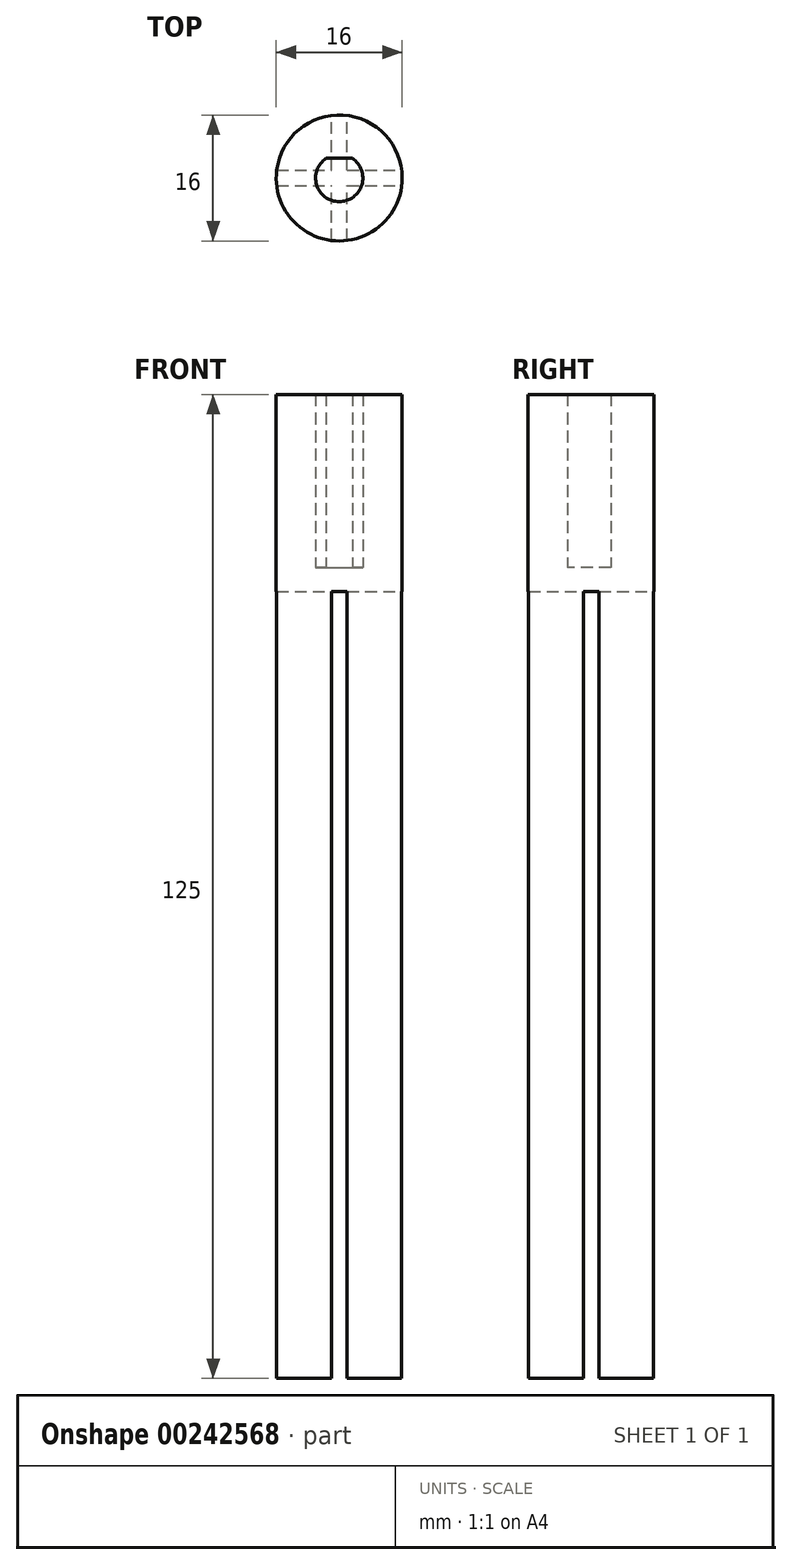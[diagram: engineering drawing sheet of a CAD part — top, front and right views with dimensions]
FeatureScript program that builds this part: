
annotation { "Feature Type Name" : "Feature", "Feature Type Description" : "" }
export const myFeature = defineFeature(function(context is Context, id is Id, definition is map)
    precondition{}
    {
        {
            var Q0;
            Q0=qCreatedBy(makeId("Top.planeOp"),FACE);
            var sketch = newSketch(context, id + "F0", { "sketchPlane" : qUnion([Q0])});
            skCircle(sketch, "E0", {"center": v(0, 0) * mm, "radius": 3 * mm});
            skLineSegment(sketch, "E1", {"start": v(-1.66, 2.5) * mm, "end": v(1.66, 2.5) * mm});
            skCircle(sketch, "E2", {"center": v(0, 0) * mm, "radius": 8 * mm});
            skSolve(sketch);
        }
        {
            var Q0;
            Q0 = qSketchRegion(id + "F0", true);
            var Q1;
            {var subQ0=sQuery(id+"F0.wireOp",EDGE,"E1");Q1=makeQuery(id+"F0.imprint","IMPRINT",FACE,{"disambiguationData":[TD([[makeQuery(id+"F0.imprint","IMPRINT",EDGE,{"derivedFrom":subQ0}),1.0]])]});}
            extrude(context, id + "F1", {"entities" : qUnion([Q0, Q1]), "depth" : 22 * mm});
        }
        {
            var Q0;
            Q0=makeQuery(id+"F1.opExtrude","CAP_FACE",FACE,{"disambiguationData":[OSD([sQuery(id+"F0.wireOp",EDGE,"E0"),sQuery(id+"F0.wireOp",EDGE,"E1"),sQuery(id+"F0.wireOp",EDGE,"E2")])],"isStart":true});
            var sketch = newSketch(context, id + "F2", { "sketchPlane" : qUnion([Q0])});
            skCircle(sketch, "E3.0", {"center": v(0, 0) * mm, "radius": 8 * mm});
            skLineSegment(sketch, "E4.bottom", {"start": v(1, -13.4) * mm, "end": v(-1, -13.4) * mm});
            skLineSegment(sketch, "E4.top", {"start": v(1, 13.4) * mm, "end": v(-1, 13.4) * mm});
            skLineSegment(sketch, "E4.left", {"start": v(1, -13.4) * mm, "end": v(1, 13.4) * mm});
            skLineSegment(sketch, "E4.right", {"start": v(-1, -13.4) * mm, "end": v(-1, 13.4) * mm});
            skLineSegment(sketch, "E5.bottom", {"start": v(16.15, 1) * mm, "end": v(-16.15, 1) * mm});
            skLineSegment(sketch, "E5.top", {"start": v(16.15, -1) * mm, "end": v(-16.15, -1) * mm});
            skLineSegment(sketch, "E5.left", {"start": v(16.15, 1) * mm, "end": v(16.15, -1) * mm});
            skLineSegment(sketch, "E5.right", {"start": v(-16.15, 1) * mm, "end": v(-16.15, -1) * mm});
            skSolve(sketch);
        }
        {
            var Q0;
            {var subQ0=sQuery(id+"F2.wireOp",EDGE,"E5.top");var subQ1=sQuery(id+"F2.wireOp",EDGE,"E4.right");var subQ2=makeQuery(id+"F2.imprint","INTERSECT",VERTEX,{"derivedFrom":[subQ1,subQ0]});Q0=makeQuery(id+"F2.imprint","IMPRINT",FACE,{"disambiguationData":[TD([[makeQuery(id+"F2.imprint","IMPRINT",EDGE,{"disambiguationData":[TD([[subQ2,1.0]])],"derivedFrom":subQ1}),1.0]])]});}
            var Q1;
            {var subQ1=sQuery(id+"F2.wireOp",EDGE,"E3.0");var subQ7=sQuery(id+"F2.wireOp",EDGE,"E4.right");var subQ8=makeQuery(id+"F2.imprint","INTERSECT",VERTEX,{"disambiguationData":[OD(0.0)],"derivedFrom":[subQ1,subQ7]});Q1=makeQuery(id+"F2.imprint","IMPRINT",FACE,{"disambiguationData":[TD([[makeQuery(id+"F2.imprint","IMPRINT",EDGE,{"disambiguationData":[TD([[subQ8,-1.0]])],"derivedFrom":subQ1}),-1.0]])]});}
            var Q2;
            {var subQ0=sQuery(id+"F2.wireOp",EDGE,"E5.bottom");var subQ1=sQuery(id+"F2.wireOp",EDGE,"E3.0");var subQ2=makeQuery(id+"F2.imprint","INTERSECT",VERTEX,{"disambiguationData":[OD(0.0)],"derivedFrom":[subQ1,subQ0]});Q2=makeQuery(id+"F2.imprint","IMPRINT",FACE,{"disambiguationData":[TD([[makeQuery(id+"F2.imprint","IMPRINT",EDGE,{"disambiguationData":[TD([[subQ2,-1.0]])],"derivedFrom":subQ1}),-1.0]])]});}
            var Q3;
            {var subQ0=sQuery(id+"F2.wireOp",EDGE,"E5.bottom");var subQ1=sQuery(id+"F2.wireOp",EDGE,"E4.right");var subQ2=makeQuery(id+"F2.imprint","INTERSECT",VERTEX,{"derivedFrom":[subQ1,subQ0]});Q3=makeQuery(id+"F2.imprint","IMPRINT",FACE,{"disambiguationData":[TD([[makeQuery(id+"F2.imprint","IMPRINT",EDGE,{"disambiguationData":[TD([[subQ2,-1.0]])],"derivedFrom":subQ1}),1.0]])]});}
            var Q4;
            {var subQ0=sQuery(id+"F2.wireOp",EDGE,"E4.left");var subQ1=sQuery(id+"F2.wireOp",EDGE,"E3.0");var subQ2=makeQuery(id+"F2.imprint","INTERSECT",VERTEX,{"disambiguationData":[OD(1.0)],"derivedFrom":[subQ1,subQ0]});Q4=makeQuery(id+"F2.imprint","IMPRINT",FACE,{"disambiguationData":[TD([[makeQuery(id+"F2.imprint","IMPRINT",EDGE,{"disambiguationData":[TD([[subQ2,-1.0]])],"derivedFrom":subQ1}),-1.0]])]});}
            var Q5;
            {var subQ0=sQuery(id+"F2.wireOp",EDGE,"E5.bottom");var subQ1=sQuery(id+"F2.wireOp",EDGE,"E4.left");var subQ2=makeQuery(id+"F2.imprint","INTERSECT",VERTEX,{"derivedFrom":[subQ1,subQ0]});Q5=makeQuery(id+"F2.imprint","IMPRINT",FACE,{"disambiguationData":[TD([[makeQuery(id+"F2.imprint","IMPRINT",EDGE,{"disambiguationData":[TD([[subQ2,-1.0]])],"derivedFrom":subQ1}),-1.0]])]});}
            var Q6;
            {var subQ5=sQuery(id+"F2.wireOp",EDGE,"E3.0");var subQ7=sQuery(id+"F2.wireOp",EDGE,"E4.left");var subQ8=makeQuery(id+"F2.imprint","INTERSECT",VERTEX,{"disambiguationData":[OD(0.0)],"derivedFrom":[subQ5,subQ7]});Q6=makeQuery(id+"F2.imprint","IMPRINT",FACE,{"disambiguationData":[TD([[makeQuery(id+"F2.imprint","IMPRINT",EDGE,{"disambiguationData":[TD([[subQ8,1.0]])],"derivedFrom":subQ5}),-1.0]])]});}
            var Q7;
            {var subQ0=sQuery(id+"F2.wireOp",EDGE,"E5.top");var subQ1=sQuery(id+"F2.wireOp",EDGE,"E4.left");var subQ2=makeQuery(id+"F2.imprint","INTERSECT",VERTEX,{"derivedFrom":[subQ1,subQ0]});Q7=makeQuery(id+"F2.imprint","IMPRINT",FACE,{"disambiguationData":[TD([[makeQuery(id+"F2.imprint","IMPRINT",EDGE,{"disambiguationData":[TD([[subQ2,1.0]])],"derivedFrom":subQ1}),-1.0]])]});}
            var Q8;
            {var subQ0=sQuery(id+"F2.wireOp",EDGE,"E4.left");var subQ1=sQuery(id+"F2.wireOp",EDGE,"E3.0");var subQ2=makeQuery(id+"F2.imprint","INTERSECT",VERTEX,{"disambiguationData":[OD(0.0)],"derivedFrom":[subQ1,subQ0]});Q8=makeQuery(id+"F2.imprint","IMPRINT",FACE,{"disambiguationData":[TD([[makeQuery(id+"F2.imprint","IMPRINT",EDGE,{"disambiguationData":[TD([[subQ2,-1.0]])],"derivedFrom":subQ1}),-1.0]])]});}
            var Q9;
            {var subQ0=sQuery(id+"F2.wireOp",EDGE,"E5.top");var subQ1=sQuery(id+"F2.wireOp",EDGE,"E4.left");var subQ2=makeQuery(id+"F2.imprint","INTERSECT",VERTEX,{"derivedFrom":[subQ1,subQ0]});Q9=makeQuery(id+"F2.imprint","IMPRINT",FACE,{"disambiguationData":[TD([[makeQuery(id+"F2.imprint","IMPRINT",EDGE,{"disambiguationData":[TD([[subQ2,1.0]])],"derivedFrom":subQ1}),1.0]])]});}
            var Q10;
            {var subQ0=sQuery(id+"F2.wireOp",EDGE,"E5.top");var subQ1=sQuery(id+"F2.wireOp",EDGE,"E3.0");var subQ2=makeQuery(id+"F2.imprint","INTERSECT",VERTEX,{"disambiguationData":[OD(1.0)],"derivedFrom":[subQ1,subQ0]});Q10=makeQuery(id+"F2.imprint","IMPRINT",FACE,{"disambiguationData":[TD([[makeQuery(id+"F2.imprint","IMPRINT",EDGE,{"disambiguationData":[TD([[subQ2,-1.0]])],"derivedFrom":subQ1}),-1.0]])]});}
            var Q11;
            {var subQ0=sQuery(id+"F2.wireOp",EDGE,"E5.top");var subQ1=sQuery(id+"F2.wireOp",EDGE,"E4.right");var subQ2=makeQuery(id+"F2.imprint","INTERSECT",VERTEX,{"derivedFrom":[subQ1,subQ0]});Q11=makeQuery(id+"F2.imprint","IMPRINT",FACE,{"disambiguationData":[TD([[makeQuery(id+"F2.imprint","IMPRINT",EDGE,{"disambiguationData":[TD([[subQ2,-1.0]])],"derivedFrom":subQ1}),1.0]])]});}
            var Q12;
            {var subQ0=sQuery(id+"F2.wireOp",EDGE,"E5.top");var subQ1=sQuery(id+"F2.wireOp",EDGE,"E3.0");var subQ2=makeQuery(id+"F2.imprint","INTERSECT",VERTEX,{"disambiguationData":[OD(0.0)],"derivedFrom":[subQ1,subQ0]});Q12=makeQuery(id+"F2.imprint","IMPRINT",FACE,{"disambiguationData":[TD([[makeQuery(id+"F2.imprint","IMPRINT",EDGE,{"disambiguationData":[TD([[subQ2,1.0]])],"derivedFrom":subQ1}),-1.0]])]});}
            var Q13;
            {var subQ0=sQuery(id+"F2.wireOp",EDGE,"E5.top");var subQ1=sQuery(id+"F2.wireOp",EDGE,"E4.left");var subQ2=makeQuery(id+"F2.imprint","INTERSECT",VERTEX,{"derivedFrom":[subQ1,subQ0]});Q13=makeQuery(id+"F2.imprint","IMPRINT",FACE,{"disambiguationData":[TD([[makeQuery(id+"F2.imprint","IMPRINT",EDGE,{"disambiguationData":[TD([[subQ2,-1.0]])],"derivedFrom":subQ1}),-1.0]])]});}
            var Q14;
            {var subQ0=sQuery(id+"F2.wireOp",EDGE,"E4.right");var subQ1=sQuery(id+"F2.wireOp",EDGE,"E3.0");var subQ2=makeQuery(id+"F2.imprint","INTERSECT",VERTEX,{"disambiguationData":[OD(1.0)],"derivedFrom":[subQ1,subQ0]});Q14=makeQuery(id+"F2.imprint","IMPRINT",FACE,{"disambiguationData":[TD([[makeQuery(id+"F2.imprint","IMPRINT",EDGE,{"disambiguationData":[TD([[subQ2,-1.0]])],"derivedFrom":subQ1}),-1.0]])]});}
            var Q15;
            {var subQ0=sQuery(id+"F2.wireOp",EDGE,"E5.bottom");var subQ1=sQuery(id+"F2.wireOp",EDGE,"E4.left");var subQ2=makeQuery(id+"F2.imprint","INTERSECT",VERTEX,{"derivedFrom":[subQ1,subQ0]});Q15=makeQuery(id+"F2.imprint","IMPRINT",FACE,{"disambiguationData":[TD([[makeQuery(id+"F2.imprint","IMPRINT",EDGE,{"disambiguationData":[TD([[subQ2,-1.0]])],"derivedFrom":subQ1}),1.0]])]});}
            var Q16;
            {var subQ0=sQuery(id+"F2.wireOp",EDGE,"E5.top");var subQ1=sQuery(id+"F2.wireOp",EDGE,"E4.left");var subQ2=makeQuery(id+"F2.imprint","INTERSECT",VERTEX,{"derivedFrom":[subQ1,subQ0]});Q16=makeQuery(id+"F2.imprint","IMPRINT",FACE,{"disambiguationData":[TD([[makeQuery(id+"F2.imprint","IMPRINT",EDGE,{"disambiguationData":[TD([[subQ2,-1.0]])],"derivedFrom":subQ1}),1.0]])]});}
            extrude(context, id + "F3", {"entities" : qUnion([Q0, Q1, Q2, Q3, Q4, Q5, Q6, Q7, Q8, Q9, Q10, Q11, Q12, Q13, Q14, Q15, Q16]), "operationType" : NewBodyOperationType.ADD, "depth" : 3 * mm});
        }
        {
            var Q0;
            {var subQ5=sQuery(id+"F2.wireOp",EDGE,"E3.0");var subQ7=sQuery(id+"F2.wireOp",EDGE,"E4.left");var subQ8=makeQuery(id+"F2.imprint","INTERSECT",VERTEX,{"disambiguationData":[OD(0.0)],"derivedFrom":[subQ5,subQ7]});Q0=makeQuery(id+"F2.imprint","IMPRINT",FACE,{"disambiguationData":[TD([[makeQuery(id+"F2.imprint","IMPRINT",EDGE,{"disambiguationData":[TD([[subQ8,1.0]])],"derivedFrom":subQ5}),-1.0]])]});}
            var Q1;
            {var subQ0=sQuery(id+"F2.wireOp",EDGE,"E5.top");var subQ1=sQuery(id+"F2.wireOp",EDGE,"E4.left");var subQ2=makeQuery(id+"F2.imprint","INTERSECT",VERTEX,{"derivedFrom":[subQ1,subQ0]});Q1=makeQuery(id+"F2.imprint","IMPRINT",FACE,{"disambiguationData":[TD([[makeQuery(id+"F2.imprint","IMPRINT",EDGE,{"disambiguationData":[TD([[subQ2,1.0]])],"derivedFrom":subQ1}),-1.0]])]});}
            var Q2;
            {var subQ1=sQuery(id+"F2.wireOp",EDGE,"E3.0");var subQ7=sQuery(id+"F2.wireOp",EDGE,"E4.right");var subQ8=makeQuery(id+"F2.imprint","INTERSECT",VERTEX,{"disambiguationData":[OD(0.0)],"derivedFrom":[subQ1,subQ7]});Q2=makeQuery(id+"F2.imprint","IMPRINT",FACE,{"disambiguationData":[TD([[makeQuery(id+"F2.imprint","IMPRINT",EDGE,{"disambiguationData":[TD([[subQ8,-1.0]])],"derivedFrom":subQ1}),-1.0]])]});}
            var Q3;
            {var subQ0=sQuery(id+"F2.wireOp",EDGE,"E5.top");var subQ1=sQuery(id+"F2.wireOp",EDGE,"E4.right");var subQ2=makeQuery(id+"F2.imprint","INTERSECT",VERTEX,{"derivedFrom":[subQ1,subQ0]});Q3=makeQuery(id+"F2.imprint","IMPRINT",FACE,{"disambiguationData":[TD([[makeQuery(id+"F2.imprint","IMPRINT",EDGE,{"disambiguationData":[TD([[subQ2,1.0]])],"derivedFrom":subQ1}),1.0]])]});}
            var Q4;
            {var subQ0=sQuery(id+"F2.wireOp",EDGE,"E5.bottom");var subQ1=sQuery(id+"F2.wireOp",EDGE,"E3.0");var subQ2=makeQuery(id+"F2.imprint","INTERSECT",VERTEX,{"disambiguationData":[OD(0.0)],"derivedFrom":[subQ1,subQ0]});Q4=makeQuery(id+"F2.imprint","IMPRINT",FACE,{"disambiguationData":[TD([[makeQuery(id+"F2.imprint","IMPRINT",EDGE,{"disambiguationData":[TD([[subQ2,-1.0]])],"derivedFrom":subQ1}),-1.0]])]});}
            var Q5;
            {var subQ0=sQuery(id+"F2.wireOp",EDGE,"E5.bottom");var subQ1=sQuery(id+"F2.wireOp",EDGE,"E4.right");var subQ2=makeQuery(id+"F2.imprint","INTERSECT",VERTEX,{"derivedFrom":[subQ1,subQ0]});Q5=makeQuery(id+"F2.imprint","IMPRINT",FACE,{"disambiguationData":[TD([[makeQuery(id+"F2.imprint","IMPRINT",EDGE,{"disambiguationData":[TD([[subQ2,-1.0]])],"derivedFrom":subQ1}),1.0]])]});}
            var Q6;
            {var subQ0=sQuery(id+"F2.wireOp",EDGE,"E5.bottom");var subQ1=sQuery(id+"F2.wireOp",EDGE,"E4.left");var subQ2=makeQuery(id+"F2.imprint","INTERSECT",VERTEX,{"derivedFrom":[subQ1,subQ0]});Q6=makeQuery(id+"F2.imprint","IMPRINT",FACE,{"disambiguationData":[TD([[makeQuery(id+"F2.imprint","IMPRINT",EDGE,{"disambiguationData":[TD([[subQ2,-1.0]])],"derivedFrom":subQ1}),-1.0]])]});}
            var Q7;
            {var subQ0=sQuery(id+"F2.wireOp",EDGE,"E4.left");var subQ1=sQuery(id+"F2.wireOp",EDGE,"E3.0");var subQ2=makeQuery(id+"F2.imprint","INTERSECT",VERTEX,{"disambiguationData":[OD(1.0)],"derivedFrom":[subQ1,subQ0]});Q7=makeQuery(id+"F2.imprint","IMPRINT",FACE,{"disambiguationData":[TD([[makeQuery(id+"F2.imprint","IMPRINT",EDGE,{"disambiguationData":[TD([[subQ2,-1.0]])],"derivedFrom":subQ1}),-1.0]])]});}
            extrude(context, id + "F4", {"entities" : qUnion([Q0, Q1, Q2, Q3, Q4, Q5, Q6, Q7]), "operationType" : NewBodyOperationType.ADD, "depth" : 103 * mm});
        }
    });
